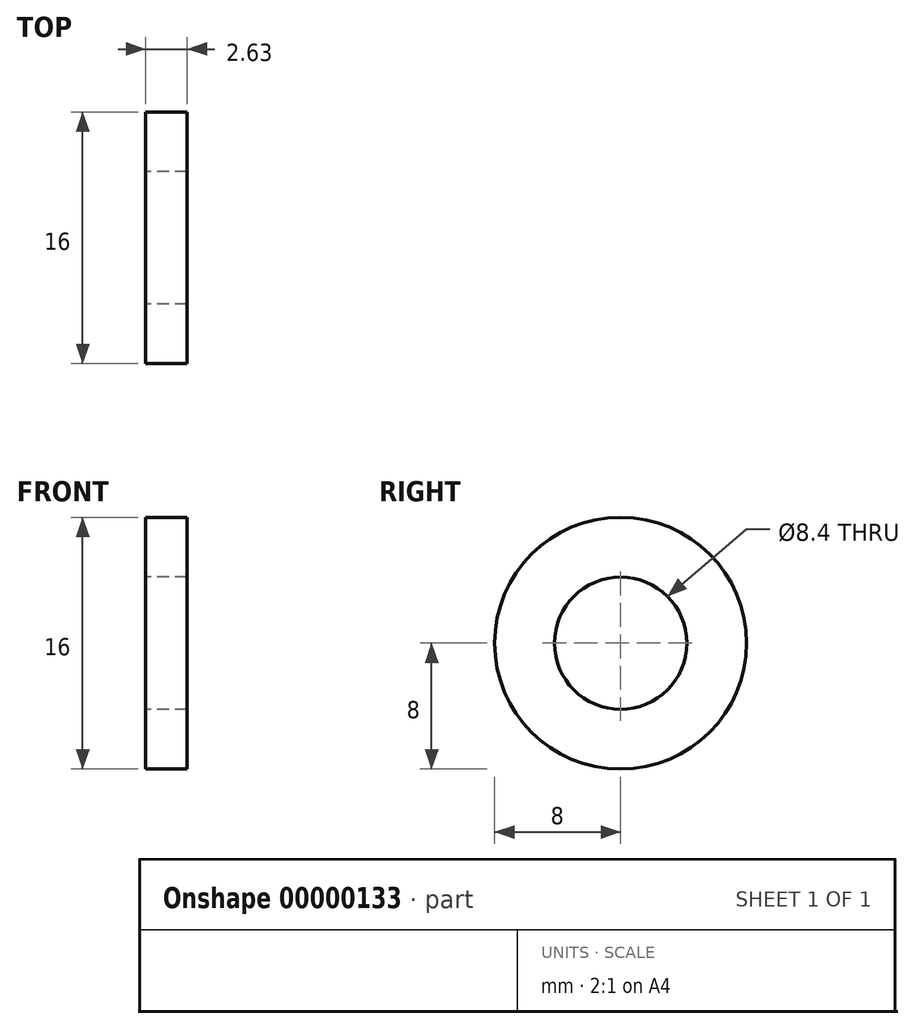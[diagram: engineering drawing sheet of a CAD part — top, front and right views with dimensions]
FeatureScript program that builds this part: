
annotation { "Feature Type Name" : "Feature", "Feature Type Description" : "" }
export const myFeature = defineFeature(function(context is Context, id is Id, definition is map)
    precondition{}
    {
        {
            var Q0;
            Q0  = qCreatedBy(makeId("Right.planeOp"), FACE);
            var sketch = newSketch(context, id + "F0", { "sketchPlane" : qUnion([Q0])});
            skCircle(sketch, "E0", {"center": v(0, 0) * mm, "radius": 8 * mm});
            skCircle(sketch, "E1", {"center": v(0, 0) * mm, "radius": 4.2 * mm});
            skSolve(sketch);
        }
        {
            var Q0;
            Q0=makeQuery(id+"F0.imprint","IMPRINT",FACE,{"disambiguationData":[TD([[makeQuery(id+"F0.imprint","IMPRINT",EDGE,{"derivedFrom":sQuery(id+"F0.wireOp",EDGE,"E0")}),1.0]])]});
            extrude(context, id + "F1", {"entities" : qUnion([Q0]), "depth" : 2.62 * mm});
        }
    });
